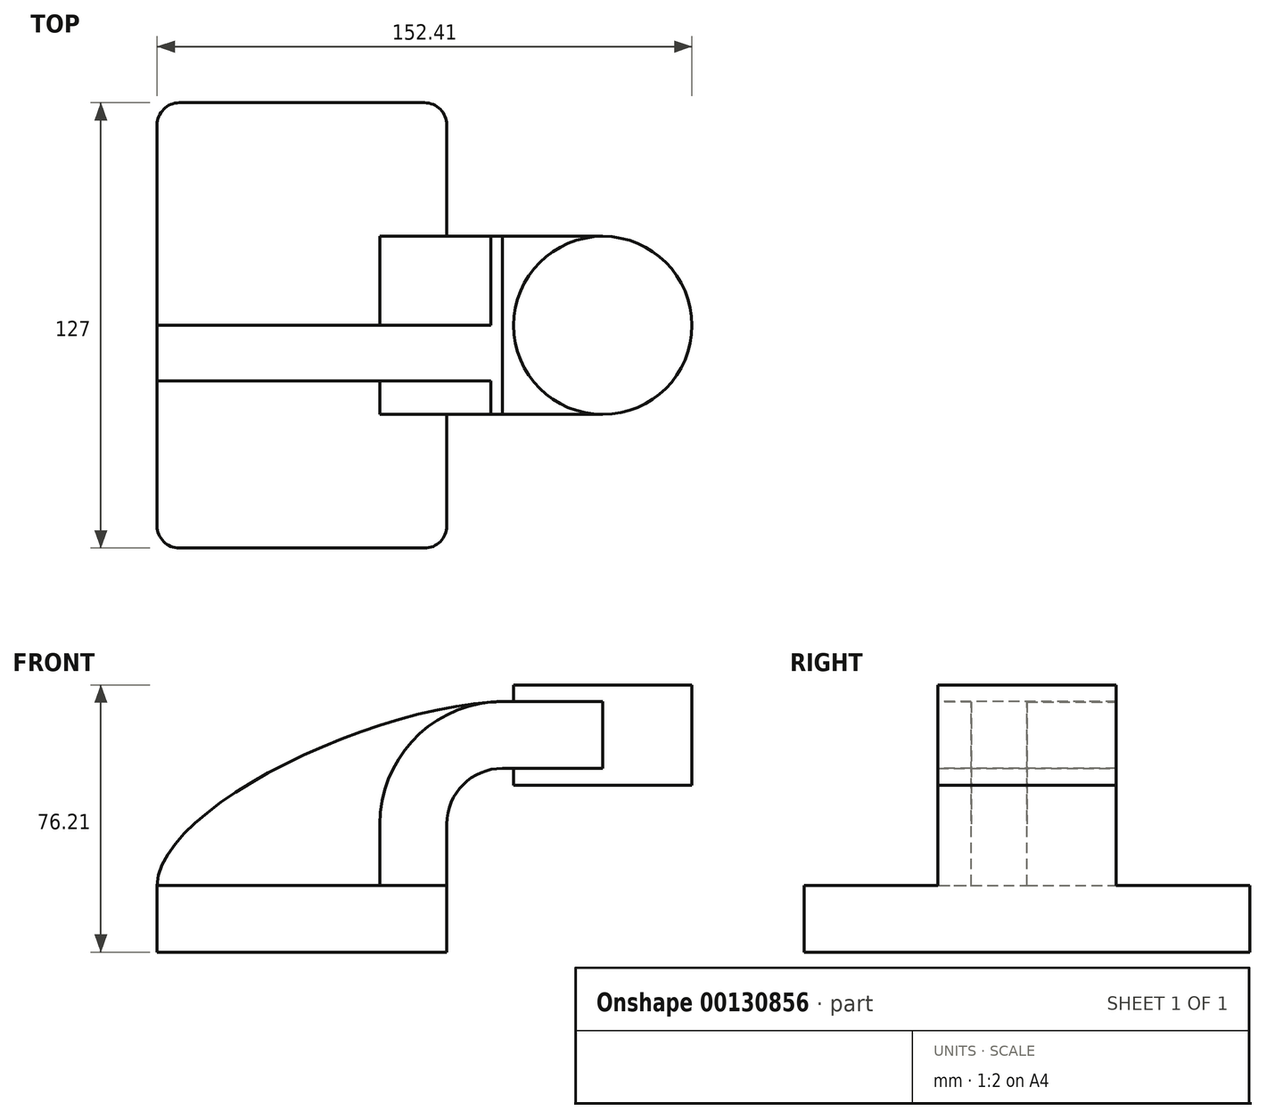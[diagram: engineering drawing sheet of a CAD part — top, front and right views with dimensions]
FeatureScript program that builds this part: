
annotation { "Feature Type Name" : "Feature", "Feature Type Description" : "" }
export const myFeature = defineFeature(function(context is Context, id is Id, definition is map)
    precondition{}
    {
        {
            var Q0;
            Q0=qCreatedBy(makeId("Front.planeOp"),FACE);
            var sketch = newSketch(context, id + "F0", { "sketchPlane" : qUnion([Q0])});
            skLineSegment(sketch, "E0.bottom", {"start": v(41.27, 9.53) * mm, "end": v(-41.28, 9.53) * mm});
            skLineSegment(sketch, "E0.top", {"start": v(41.28, -9.52) * mm, "end": v(-41.27, -9.52) * mm});
            skLineSegment(sketch, "E0.left", {"start": v(41.28, 9.53) * mm, "end": v(41.28, -9.52) * mm});
            skLineSegment(sketch, "E0.right", {"start": v(-41.28, 9.53) * mm, "end": v(-41.27, -9.52) * mm});
            skPoint(sketch, "E0.middle", {"position": v(0, 0) * mm});
            skLineSegment(sketch, "E1.bottom", {"start": v(111.12, 38.1) * mm, "end": v(60.32, 38.1) * mm});
            skLineSegment(sketch, "E1.top", {"start": v(111.12, 66.68) * mm, "end": v(60.32, 66.68) * mm});
            skLineSegment(sketch, "E1.left", {"start": v(111.12, 38.1) * mm, "end": v(111.12, 66.68) * mm});
            skLineSegment(sketch, "E1.right", {"start": v(60.32, 38.1) * mm, "end": v(60.32, 66.68) * mm});
            skPoint(sketch, "E1.middle", {"position": v(85.72, 52.39) * mm});
            skLineSegment(sketch, "E2", {"start": v(41.27, 9.53) * mm, "end": v(41.27, 27) * mm});
            skArc(sketch, "E3", {"start": v(41.27, 27) * mm, "mid": v(45.92, 38.23) * mm, "end": v(57.15, 42.88) * mm});
            skLineSegment(sketch, "E4", {"start": v(57.15, 42.88) * mm, "end": v(85.65, 42.88) * mm});
            skLineSegment(sketch, "E5.0", {"start": v(57.15, 61.93) * mm, "end": v(85.65, 61.93) * mm});
            skArc(sketch, "E5.1", {"start": v(22.23, 27) * mm, "mid": v(32.45, 51.7) * mm, "end": v(57.15, 61.93) * mm});
            skLineSegment(sketch, "E5.2", {"start": v(22.22, 9.53) * mm, "end": v(22.22, 27) * mm});
            skLineSegment(sketch, "E6", {"start": v(85.65, 61.93) * mm, "end": v(85.65, 42.88) * mm});
            skLineSegment(sketch, "E7", {"start": v(22.22, 9.53) * mm, "end": v(41.27, 9.53) * mm});
            skFitSpline(sketch, "E8", {"points": [v(-41.28, 9.52) * mm, v(57.15, 61.93) * mm], "startDerivative": vector(1.9, 67.33) * mm, "endDerivative": vector(108.3, 2.77) * mm});
            skLineSegment(sketch, "E9", {"start": v(85.72, 66.68) * mm, "end": v(85.72, 38.1) * mm});
            skLineSegment(sketch, "E10", {"start": v(85.72, 38.1) * mm, "end": v(85.72, 52.39) * mm});
            skSolve(sketch);
        }
        {
            var Q0;
            Q0=makeQuery(id+"F0.imprint","IMPRINT",FACE,{"disambiguationData":[TD([[makeQuery(id+"F0.imprint","IMPRINT",EDGE,{"derivedFrom":sQuery(id+"F0.wireOp",EDGE,"E0.bottom")}),1.0]])]});
            extrude(context, id + "F1", {"entities" : qUnion([Q0]), "depth" : 127 * mm, "symmetric" : true});
        }
        {
            var Q0;
            {var subQ5=sQuery(id+"F0.wireOp",EDGE,"E6");Q0=makeQuery(id+"F0.imprint","IMPRINT",FACE,{"disambiguationData":[TD([[makeQuery(id+"F0.imprint","IMPRINT",EDGE,{"derivedFrom":subQ5}),-1.0]])]});}
            var Q1;
            Q1=makeQuery(id+"F0.imprint","IMPRINT",FACE,{"disambiguationData":[TD([[makeQuery(id+"F0.imprint","IMPRINT",EDGE,{"derivedFrom":sQuery(id+"F0.wireOp",EDGE,"E2")}),1.0]])]});
            extrude(context, id + "F2", {"entities" : qUnion([Q0, Q1]), "operationType" : NewBodyOperationType.ADD, "depth" : 50.8 * mm, "symmetric" : true});
        }
        {
            var Q0;
            {var subQ0=sQuery(id+"F0.wireOp",EDGE,"E0.bottom");Q0=makeQuery(id+"F0.imprint","IMPRINT",FACE,{"disambiguationData":[TD([[makeQuery(id+"F0.imprint","IMPRINT",EDGE,{"derivedFrom":subQ0}),-1.0]])]});}
            extrude(context, id + "F3", {"entities" : qUnion([Q0]), "operationType" : NewBodyOperationType.ADD, "depth" : 15.88 * mm});
        }
        {
            var Q0;
            {var subQ1=sQuery(id+"F0.wireOp",EDGE,"E1.left");Q0=makeQuery(id+"F0.imprint","IMPRINT",FACE,{"disambiguationData":[TD([[makeQuery(id+"F0.imprint","IMPRINT",EDGE,{"derivedFrom":subQ1}),1.0]])]});}
            var Q1;
            Q1=sQuery(id+"F0.wireOp",EDGE,"E9");
            revolve(context, id + "F4", {"operationType" : NewBodyOperationType.ADD, "entities" : qUnion([Q0]), "axis" : qUnion([Q1]), "revolveType" : RevolveType.FULL});
        }
        {
            var Q0;
            Q0=makeQuery(id+"F1.opExtrude","CAP_EDGE",EDGE,{"disambiguationData":[OSD([sQuery(id+"F0.wireOp",EDGE,"E0.left")])],"isStart":true});
            var Q1;
            Q1=makeQuery(id+"F1.opExtrude","CAP_EDGE",EDGE,{"disambiguationData":[OSD([sQuery(id+"F0.wireOp",EDGE,"E0.right")])],"isStart":true});
            var Q2;
            Q2=makeQuery(id+"F1.opExtrude","CAP_EDGE",EDGE,{"disambiguationData":[OSD([sQuery(id+"F0.wireOp",EDGE,"E0.left")])],"isStart":false});
            var Q3;
            Q3=makeQuery(id+"F1.opExtrude","CAP_EDGE",EDGE,{"disambiguationData":[OSD([sQuery(id+"F0.wireOp",EDGE,"E0.right")])],"isStart":false});
            fillet(context, id + "F5", {"entities" : qUnion([Q0, Q1, Q2, Q3]), "radius" : 6.35 * mm, "tangentPropagation" : true, "allowEdgeOverflow" : false});
        }
    });
